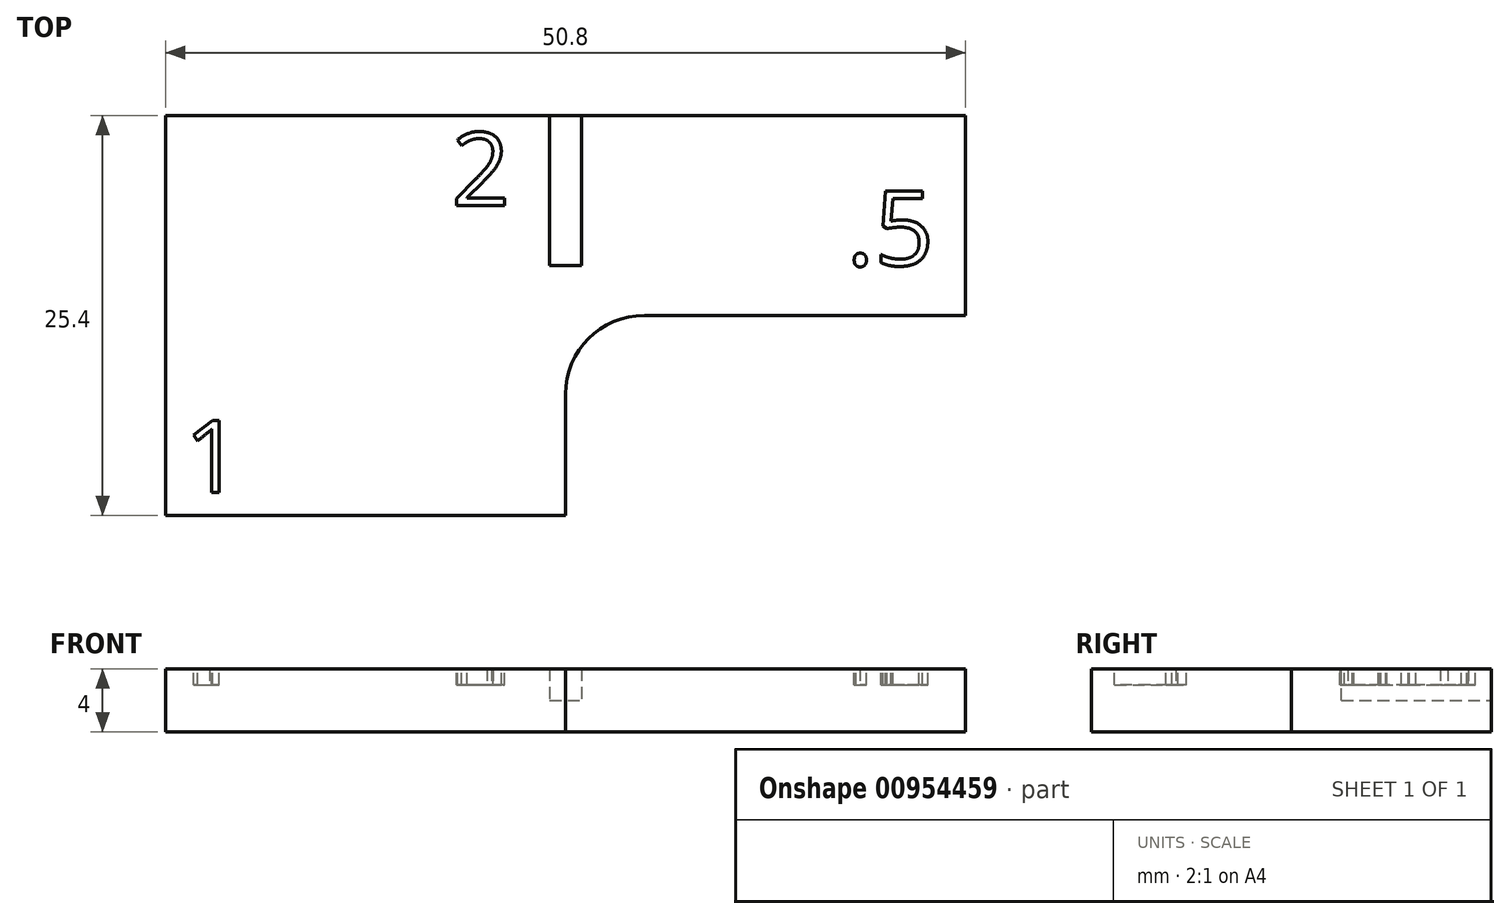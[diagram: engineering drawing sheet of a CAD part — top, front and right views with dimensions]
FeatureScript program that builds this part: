
annotation { "Feature Type Name" : "Feature", "Feature Type Description" : "" }
export const myFeature = defineFeature(function(context is Context, id is Id, definition is map)
    precondition{}
    {
        {
            var Q0;
            Q0=qCreatedBy(makeId("Top.planeOp"),FACE);
            var sketch = newSketch(context, id + "F0", { "sketchPlane" : qUnion([Q0])});
            skLineSegment(sketch, "E0.top", {"start": v(-12.7, -12.7) * mm, "end": v(12.7, -12.7) * mm});
            skLineSegment(sketch, "E0.left", {"start": v(-12.7, 12.7) * mm, "end": v(-12.7, -12.7) * mm});
            skPoint(sketch, "E0.middle", {"position": v(0, 0) * mm});
            skLineSegment(sketch, "E1.top", {"start": v(17.7, 0) * mm, "end": v(38.1, 0) * mm});
            skLineSegment(sketch, "E1.right", {"start": v(38.1, 12.7) * mm, "end": v(38.1, 0) * mm});
            skLineSegment(sketch, "E2", {"start": v(12.7, -12.7) * mm, "end": v(12.7, -5) * mm});
            skPoint(sketch, "E3.visualSharp", {"position": v(12.7, 0) * mm});
            skArc(sketch, "E3.filletArc", {"start": v(17.7, 0) * mm, "mid": v(14.16, -1.46) * mm, "end": v(12.7, -5) * mm});
            skLineSegment(sketch, "E4", {"start": v(-12.7, 12.7) * mm, "end": v(38.1, 12.7) * mm});
            skSolve(sketch);
        }
        {
            var Q0;
            Q0=qSketchRegion(id+"F0",true);
            extrude(context, id + "F1", {"entities" : qUnion([Q0]), "depth" : 4 * mm, "offsetDistance" : 25 * mm});
        }
        {
            var Q0;
            Q0=makeQuery(id+"F1.opExtrude","CAP_FACE",FACE,{"disambiguationData":[OSD([sQuery(id+"F0.wireOp",EDGE,"E0.bottom"),sQuery(id+"F0.wireOp",EDGE,"E0.top"),sQuery(id+"F0.wireOp",EDGE,"E0.left"),sQuery(id+"F0.wireOp",EDGE,"E1.bottom"),sQuery(id+"F0.wireOp",EDGE,"E1.top"),sQuery(id+"F0.wireOp",EDGE,"E1.right"),sQuery(id+"F0.wireOp",EDGE,"E2"),sQuery(id+"F0.wireOp",EDGE,"E3.filletArc")])],"isStart":false});
            var sketch = newSketch(context, id + "F2", { "sketchPlane" : qUnion([Q0])});
            skLineSegment(sketch, "E5.bottom", {"start": v(13.7, 3.17) * mm, "end": v(11.7, 3.17) * mm});
            skLineSegment(sketch, "E5.top", {"start": v(13.7, 22.22) * mm, "end": v(11.7, 22.22) * mm});
            skLineSegment(sketch, "E5.left", {"start": v(13.7, 3.17) * mm, "end": v(13.7, 22.22) * mm});
            skLineSegment(sketch, "E5.right", {"start": v(11.7, 3.17) * mm, "end": v(11.7, 22.22) * mm});
            skPoint(sketch, "E5.middle", {"position": v(12.7, 12.7) * mm});
            skSolve(sketch);
        }
        {
            var Q0;
            Q0=qSketchRegion(id+"F2",true);
            extrude(context, id + "F3", {"entities" : qUnion([Q0]), "operationType" : NewBodyOperationType.REMOVE, "oppositeDirection" : true, "depth" : 2 * mm, "offsetDistance" : 25 * mm});
        }
        {
            var Q0;
            Q0=makeQuery(id+"F1.opExtrude","CAP_FACE",FACE,{"disambiguationData":[OSD([sQuery(id+"F0.wireOp",EDGE,"E0.bottom"),sQuery(id+"F0.wireOp",EDGE,"E0.top"),sQuery(id+"F0.wireOp",EDGE,"E0.left"),sQuery(id+"F0.wireOp",EDGE,"E1.bottom"),sQuery(id+"F0.wireOp",EDGE,"E1.top"),sQuery(id+"F0.wireOp",EDGE,"E1.right"),sQuery(id+"F0.wireOp",EDGE,"E2"),sQuery(id+"F0.wireOp",EDGE,"E3.filletArc")])],"isStart":false});
            var sketch = newSketch(context, id + "F4", { "sketchPlane" : qUnion([Q0])});
            skText(sketch, "E6", { "text": ".5", "fontName": "OpenSans-Regular.ttf"});
            skText(sketch, "E7", { "text": "2", "fontName": "OpenSans-Regular.ttf"});
            skText(sketch, "E8", { "text": "1", "fontName": "OpenSans-Regular.ttf"});
            const initialGuessF4  = {"E6": [0.03054, 0.00318, 1, 0, 0.00477], "E7": [0.00545, 0.00698, 1, 0, 0.00468], "E8": [-0.01152, -0.01123, 1, 0, 0.0046]};
            skSetInitialGuess(sketch, initialGuessF4);
            skSolve(sketch);
        }
        {
            var Q0;
            Q0=qSketchRegion(id+"F4",true);
            extrude(context, id + "F5", {"entities" : qUnion([Q0]), "operationType" : NewBodyOperationType.REMOVE, "oppositeDirection" : true, "depth" : 1 * mm, "offsetDistance" : 25 * mm});
        }
    });
